# Revit family: Gewindestange_TR_M6_M8_M10_M12_2M_G
name_source: partatom
category: Generic Models
revit_build: Autodesk Revit 2017 (Build: 20190508_0315(x64)
units: mm (PartAtom-declared; Revit-internal decimal feet)

## family parameters
Always vertical = Yes
Can host rebar = No
Cut with Voids When Loaded = No
Part Type = Normal
Room Calculation Point = No
Round Connector Dimension = Use Diameter
Shared = No
Work Plane-Based = No

## types (4) — shared parameters
Manufacturer = OBO BETTERMANN
Material = Elektrogalvanised
URL = http://www.obo-bettermann.com

## per-type parameters (varying)
| type | Diameter | GTIN | Manufacturer Art.No. |
| TR M6 2M G | 6 mm  [stored 0.019685 ft] | 4012196096640 | 3141048 |
| TR M8 2M G | 8 mm  [stored 0.0262467 ft] | 4012195119982 | 3141136 |
| TR M10 2M G | 10 mm  [stored 0.0328084 ft] | 4012195123583 | 3141140 |
| TR M12 2M G | 12 mm  [stored 0.0393701 ft] | 4012195123644 | 3141144 |

note: column(s) folded — value = type name in every type: Article Type

note: [stored X ft] marks values corroborated as IEEE doubles in the binary element streams (Revit-internal decimal feet)

## geometry (parser evidence)
native form markers: Sweep x3
no freeform markers — native parametric forms only
